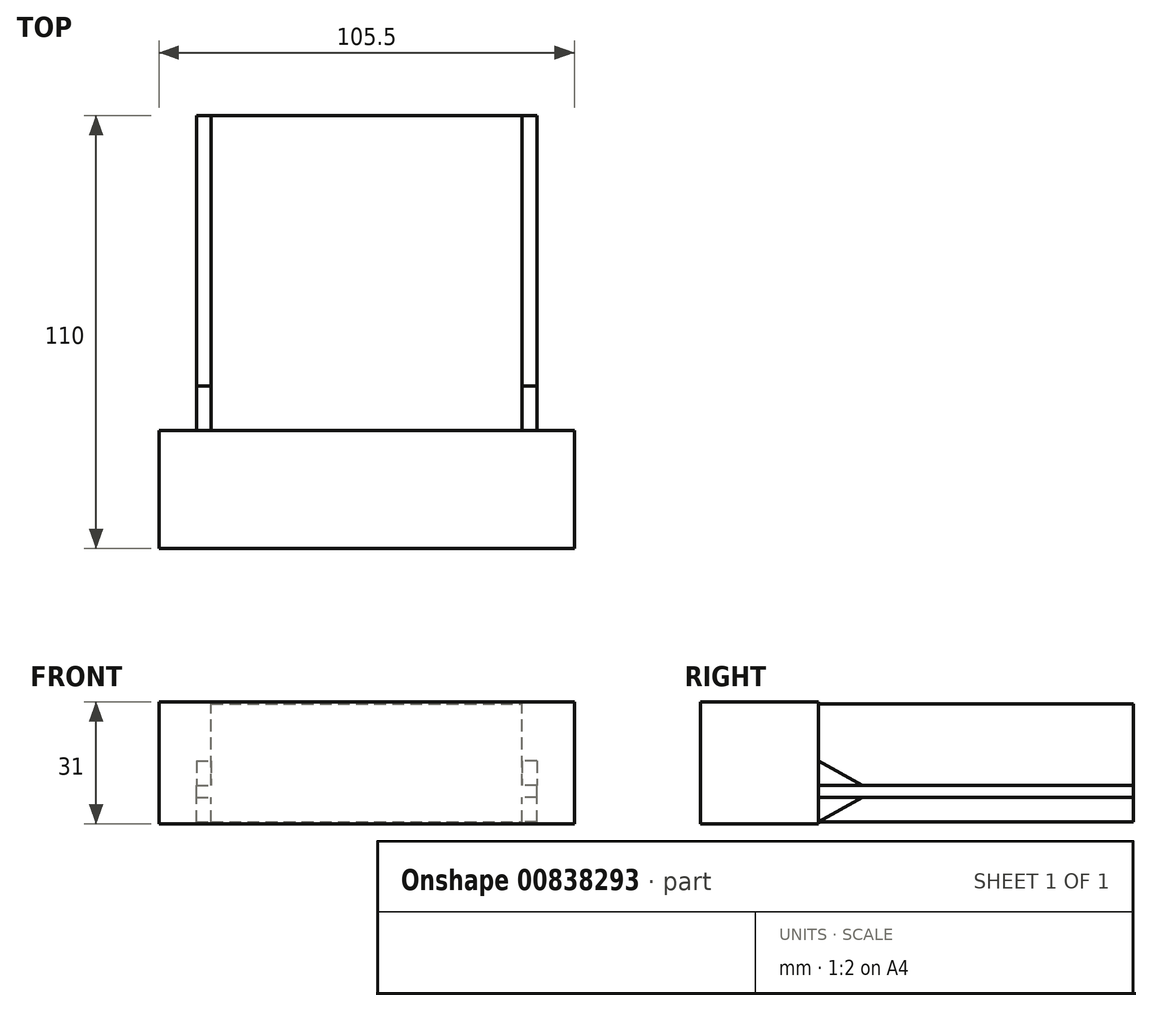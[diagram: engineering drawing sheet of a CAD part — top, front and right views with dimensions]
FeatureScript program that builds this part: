
annotation { "Feature Type Name" : "Feature", "Feature Type Description" : "" }
export const myFeature = defineFeature(function(context is Context, id is Id, definition is map)
    precondition{}
    {
        {
            var Q0;
            Q0=qCreatedBy(makeId("Front.planeOp"),FACE);
            var sketch = newSketch(context, id + "F0", { "sketchPlane" : qUnion([Q0])});
            skLineSegment(sketch, "E0.bottom", {"start": v(-39.5, -15) * mm, "end": v(39.5, -15) * mm});
            skLineSegment(sketch, "E0.top", {"start": v(-39.5, 15) * mm, "end": v(39.5, 15) * mm});
            skLineSegment(sketch, "E0.left", {"start": v(-39.5, -15) * mm, "end": v(-39.5, 15) * mm});
            skLineSegment(sketch, "E0.right", {"start": v(39.5, -15) * mm, "end": v(39.5, 15) * mm});
            skPoint(sketch, "E0.middle", {"position": v(0, 0) * mm});
            skSolve(sketch);
        }
        {
            var Q0;
            Q0=makeQuery(id+"F0.imprint","IMPRINT",FACE,{"disambiguationData":[TD([[makeQuery(id+"F0.imprint","IMPRINT",EDGE,{"derivedFrom":sQuery(id+"F0.wireOp",EDGE,"E0.bottom")}),1.0]])]});
            extrude(context, id + "F1", {"entities" : qUnion([Q0]), "depth" : -80 * mm, "offsetDistance" : 25 * mm});
        }
        {
            var Q0;
            Q0=makeQuery(id+"F1.opExtrude","CAP_FACE",FACE,{"disambiguationData":[OSD([sQuery(id+"F0.wireOp",EDGE,"E0.bottom"),sQuery(id+"F0.wireOp",EDGE,"E0.top"),sQuery(id+"F0.wireOp",EDGE,"E0.left"),sQuery(id+"F0.wireOp",EDGE,"E0.right")])],"isStart":true});
            var sketch = newSketch(context, id + "F2", { "sketchPlane" : qUnion([Q0])});
            skLineSegment(sketch, "E1.bottom", {"start": v(-52.75, 15.5) * mm, "end": v(52.75, 15.5) * mm});
            skLineSegment(sketch, "E1.top", {"start": v(-52.75, -15.5) * mm, "end": v(52.75, -15.5) * mm});
            skLineSegment(sketch, "E1.left", {"start": v(-52.75, 15.5) * mm, "end": v(-52.75, -15.5) * mm});
            skLineSegment(sketch, "E1.right", {"start": v(52.75, 15.5) * mm, "end": v(52.75, -15.5) * mm});
            skPoint(sketch, "E1.middle", {"position": v(0, 0) * mm});
            skSolve(sketch);
        }
        {
            var Q0;
            Q0=makeQuery(id+"F2.imprint","IMPRINT",FACE,{"disambiguationData":[TD([[makeQuery(id+"F2.imprint","IMPRINT",EDGE,{"derivedFrom":sQuery(id+"F2.wireOp",EDGE,"E1.bottom")}),-1.0]])]});
            extrude(context, id + "F3", {"entities" : qUnion([Q0]), "depth" : 30 * mm, "offsetDistance" : 25 * mm});
        }
        {
            var Q0;
            Q0=makeQuery(id+"F2.imprint","IMPRINT",FACE,{"disambiguationData":[TD([[makeQuery(id+"F2.imprint","IMPRINT",EDGE,{"derivedFrom":makeQuery(id+"F1.opExtrude","CAP_EDGE",EDGE,{"disambiguationData":[OSD([sQuery(id+"F0.wireOp",EDGE,"E0.bottom")])],"isStart":true})}),1.0]])]});
            var Q1;
            Q1=makeQuery(id+"F3.opExtrude","CAP_FACE",FACE,{"disambiguationData":[OSD([sQuery(id+"F0.wireOp",EDGE,"E0.bottom"),sQuery(id+"F0.wireOp",EDGE,"E0.top"),sQuery(id+"F0.wireOp",EDGE,"E0.left"),sQuery(id+"F0.wireOp",EDGE,"E0.right"),sQuery(id+"F2.wireOp",EDGE,"E1.bottom"),sQuery(id+"F2.wireOp",EDGE,"E1.top"),sQuery(id+"F2.wireOp",EDGE,"E1.left"),sQuery(id+"F2.wireOp",EDGE,"E1.right")])],"isStart":false});
            extrude(context, id + "F4", {"entities" : qUnion([Q0]), "operationType" : NewBodyOperationType.ADD, "endBound" : BoundingType.UP_TO_SURFACE, "depth" : 25 * mm, "endBoundEntityFace" : qUnion([Q1]), "offsetDistance" : 25 * mm});
        }
        {
            var Q0;
            Q0=qCreatedBy(makeId("Front.planeOp"),FACE);
            var sketch = newSketch(context, id + "F5", { "sketchPlane" : qUnion([Q0])});
            skLineSegment(sketch, "E2", {"start": v(-39.5, -8.75) * mm, "end": v(-43.25, -8.75) * mm});
            skLineSegment(sketch, "E3", {"start": v(-43.25, -8.75) * mm, "end": v(-43.25, -5.75) * mm});
            skLineSegment(sketch, "E4", {"start": v(-43.25, -5.75) * mm, "end": v(-39.5, -5.75) * mm});
            skLineSegment(sketch, "E5", {"start": v(-39.5, -5.75) * mm, "end": v(-39.5, -8.75) * mm});
            skSolve(sketch);
        }
        {
            var Q0;
            Q0=makeQuery(id+"F5.imprint","IMPRINT",FACE,{"disambiguationData":[TD([[makeQuery(id+"F5.imprint","IMPRINT",EDGE,{"derivedFrom":sQuery(id+"F5.wireOp",EDGE,"E2")}),-1.0]])]});
            var Q1;
            Q1=makeQuery(id+"F1.opExtrude","CAP_FACE",FACE,{"disambiguationData":[OSD([sQuery(id+"F0.wireOp",EDGE,"E0.bottom"),sQuery(id+"F0.wireOp",EDGE,"E0.top"),sQuery(id+"F0.wireOp",EDGE,"E0.left"),sQuery(id+"F0.wireOp",EDGE,"E0.right")])],"isStart":false});
            var Q2;
            Q2=makeQuery(id+"F1.opExtrude","SWEPT_BODY",BODY,{"disambiguationData":[OSD([sQuery(id+"F0.wireOp",EDGE,"E0.bottom"),sQuery(id+"F0.wireOp",EDGE,"E0.top"),sQuery(id+"F0.wireOp",EDGE,"E0.left"),sQuery(id+"F0.wireOp",EDGE,"E0.right")])]});
            var Q3;
            Q3 = qBodyType(qCreatedBy(id + "F7" ,FACE), BodyType.SOLID);
            extrude(context, id + "F6", {"entities" : qUnion([Q0]), "oppositeDirection" : true, "depth" : 80 * mm, "endBoundEntityFace" : qUnion([Q1]), "endBoundEntityBody" : qUnion([Q2]), "offsetDistance" : 25 * mm});
        }
        {
            var Q0;
            Q0=makeQuery(id+"F2.imprint","IMPRINT",FACE,{"disambiguationData":[TD([[makeQuery(id+"F2.imprint","IMPRINT",EDGE,{"derivedFrom":makeQuery(id+"F1.opExtrude","CAP_EDGE",EDGE,{"disambiguationData":[OSD([sQuery(id+"F0.wireOp",EDGE,"E0.bottom")])],"isStart":true})}),1.0]])]});
            cPlane(context, id + "F7", {"entities" : qUnion([Q0]), "cplaneType" : CPlaneType.OFFSET, "offset" : 80 * mm, "oppositeDirection" : true, "width" : 150 * mm, "height" : 150 * mm});
        }
        {
            var Q0;
            Q0=makeQuery(id+"F6.opExtrude","SWEPT_BODY",BODY,{"disambiguationData":[OSD([sQuery(id+"F5.wireOp",EDGE,"E2"),sQuery(id+"F5.wireOp",EDGE,"E3"),sQuery(id+"F5.wireOp",EDGE,"E4"),sQuery(id+"F5.wireOp",EDGE,"E5")])]});
            var Q1;
            Q1=makeQuery(id+"F1.opExtrude","SWEPT_FACE",FACE,{"disambiguationData":[OSD([sQuery(id+"F0.wireOp",EDGE,"E0.right")])]});
            mirror(context, id + "F8", {"entities" : qUnion([Q0]), "mirrorPlane" : qUnion([Q1])});
        }
        {
            var Q0;
            Q0=makeQuery(id+"F8.opPattern","COPY",BODY,{"derivedFrom":makeQuery(id+"F6.opExtrude","SWEPT_BODY",BODY,{"disambiguationData":[OSD([sQuery(id+"F5.wireOp",EDGE,"E2"),sQuery(id+"F5.wireOp",EDGE,"E3"),sQuery(id+"F5.wireOp",EDGE,"E4"),sQuery(id+"F5.wireOp",EDGE,"E5")])]}),"instanceName":"1"});
            var Q1;
            Q1=makeQuery(id+"F8.opPattern","COPY",FACE,{"derivedFrom":makeQuery(id+"F6.opExtrude","SWEPT_FACE",FACE,{"disambiguationData":[OSD([sQuery(id+"F5.wireOp",EDGE,"E5")])]}),"instanceName":"1"});
            var Q2;
            Q2=makeQuery(id+"F1.opExtrude","SWEPT_FACE",FACE,{"disambiguationData":[OSD([sQuery(id+"F0.wireOp",EDGE,"E0.right")])]});
            transform(context, id + "F9", {"entities" : qUnion([Q0]), "transformType" : TransformType.TRANSLATION_DISTANCE, "transformDirection" : qUnion([Q1, Q2]), "distance" : 79 * mm, "makeCopy" : false});
        }
        {
            var Q0;
            Q0=makeQuery(id+"F8.opPattern","COPY",BODY,{"derivedFrom":makeQuery(id+"F6.opExtrude","SWEPT_BODY",BODY,{"disambiguationData":[OSD([sQuery(id+"F5.wireOp",EDGE,"E2"),sQuery(id+"F5.wireOp",EDGE,"E3"),sQuery(id+"F5.wireOp",EDGE,"E4"),sQuery(id+"F5.wireOp",EDGE,"E5")])]}),"instanceName":"1"});
            var Q1;
            Q1=makeQuery(id+"F1.opExtrude","SWEPT_BODY",BODY,{"disambiguationData":[OSD([sQuery(id+"F0.wireOp",EDGE,"E0.bottom"),sQuery(id+"F0.wireOp",EDGE,"E0.top"),sQuery(id+"F0.wireOp",EDGE,"E0.left"),sQuery(id+"F0.wireOp",EDGE,"E0.right")])]});
            booleanBodies(context, id + "F10", {"operationType" : BooleanOperationType.UNION, "tools" : qUnion([Q0, Q1])});
        }
        {
            var Q0;
            Q0=makeQuery(id+"F6.opExtrude","SWEPT_BODY",BODY,{"disambiguationData":[OSD([sQuery(id+"F5.wireOp",EDGE,"E2"),sQuery(id+"F5.wireOp",EDGE,"E3"),sQuery(id+"F5.wireOp",EDGE,"E4"),sQuery(id+"F5.wireOp",EDGE,"E5")])]});
            var Q1;
            Q1=makeQuery(id+"F8.opPattern","COPY",BODY,{"derivedFrom":makeQuery(id+"F6.opExtrude","SWEPT_BODY",BODY,{"disambiguationData":[OSD([sQuery(id+"F5.wireOp",EDGE,"E2"),sQuery(id+"F5.wireOp",EDGE,"E3"),sQuery(id+"F5.wireOp",EDGE,"E4"),sQuery(id+"F5.wireOp",EDGE,"E5")])]}),"instanceName":"1"});
            booleanBodies(context, id + "F11", {"operationType" : BooleanOperationType.UNION, "tools" : qUnion([Q0, Q1])});
        }
        {
            var Q0;
            Q0=makeQuery(id+"F6.opExtrude","SWEPT_BODY",BODY,{"disambiguationData":[OSD([sQuery(id+"F5.wireOp",EDGE,"E2"),sQuery(id+"F5.wireOp",EDGE,"E3"),sQuery(id+"F5.wireOp",EDGE,"E4"),sQuery(id+"F5.wireOp",EDGE,"E5")])]});
            transform(context, id + "F12", {"entities" : qUnion([Q0]), "transformType" : TransformType.COPY});
        }
        {
            var Q0;
            Q0=makeQuery(id+"F12.opPattern","COPY",BODY,{"derivedFrom":makeQuery(id+"F6.opExtrude","SWEPT_BODY",BODY,{"disambiguationData":[OSD([sQuery(id+"F5.wireOp",EDGE,"E2"),sQuery(id+"F5.wireOp",EDGE,"E3"),sQuery(id+"F5.wireOp",EDGE,"E4"),sQuery(id+"F5.wireOp",EDGE,"E5")])]}),"instanceName":"1"});
            transform(context, id + "F13", {"entities" : qUnion([Q0]), "transformType" : TransformType.TRANSLATION_3D, "dx" : 0 * mm, "dy" : 0 * mm, "dz" : 0 * mm, "makeCopy" : true});
        }
        {
            var Q0;
            Q0=makeQuery(id+"F13.opPattern","COPY",BODY,{"derivedFrom":makeQuery(id+"F12.opPattern","COPY",BODY,{"derivedFrom":makeQuery(id+"F6.opExtrude","SWEPT_BODY",BODY,{"disambiguationData":[OSD([sQuery(id+"F5.wireOp",EDGE,"E2"),sQuery(id+"F5.wireOp",EDGE,"E3"),sQuery(id+"F5.wireOp",EDGE,"E4"),sQuery(id+"F5.wireOp",EDGE,"E5")])]}),"instanceName":"1"}),"instanceName":"1"});
            deleteBodies(context, id + "F14", {"entities" : qUnion([Q0])});
        }
        {
            var Q0;
            Q0=makeQuery(id+"F12.opPattern","COPY",BODY,{"derivedFrom":makeQuery(id+"F6.opExtrude","SWEPT_BODY",BODY,{"disambiguationData":[OSD([sQuery(id+"F5.wireOp",EDGE,"E2"),sQuery(id+"F5.wireOp",EDGE,"E3"),sQuery(id+"F5.wireOp",EDGE,"E4"),sQuery(id+"F5.wireOp",EDGE,"E5")])]}),"instanceName":"1"});
            deleteBodies(context, id + "F15", {"entities" : qUnion([Q0])});
        }
        {
            var Q0;
            {var subQ1=sQuery(id+"F0.wireOp",EDGE,"E0.left");var subQ3=sQuery(id+"F0.wireOp",EDGE,"E0.bottom");Q0=makeQuery(id+"F11.opBoolean","SPLIT",FACE,{"disambiguationData":[TD([makeQuery(id+"F1.opExtrude","SWEPT_FACE",FACE,{"disambiguationData":[OSD([subQ3])]})])],"derivedFrom":makeQuery(id+"F1.opExtrude","SWEPT_FACE",FACE,{"disambiguationData":[OSD([subQ1])]})});}
            var sketch = newSketch(context, id + "F16", { "sketchPlane" : qUnion([Q0])});
            skSolve(sketch);
        }
        {
            var Q0;
            {var subQ0=sQuery(id+"F0.wireOp",EDGE,"E0.right");var subQ3=sQuery(id+"F0.wireOp",EDGE,"E0.bottom");Q0=makeQuery(id+"F10.opBoolean","SPLIT",FACE,{"disambiguationData":[TD([makeQuery(id+"F1.opExtrude","SWEPT_FACE",FACE,{"disambiguationData":[OSD([subQ3])]})])],"derivedFrom":makeQuery(id+"F1.opExtrude","SWEPT_FACE",FACE,{"disambiguationData":[OSD([subQ0])]})});}
            var sketch = newSketch(context, id + "F17", { "sketchPlane" : qUnion([Q0])});
            skLineSegment(sketch, "E6", {"start": v(0, -15) * mm, "end": v(11.24, -8.75) * mm});
            skLineSegment(sketch, "E7", {"start": v(11.24, -8.75) * mm, "end": v(0, -8.75) * mm});
            skLineSegment(sketch, "E8", {"start": v(0, -8.75) * mm, "end": v(0, -15) * mm});
            skSolve(sketch);
        }
        {
            var Q0;
            Q0=makeQuery(id+"F17.imprint","IMPRINT",FACE,{"disambiguationData":[TD([[makeQuery(id+"F17.imprint","IMPRINT",EDGE,{"derivedFrom":sQuery(id+"F17.wireOp",EDGE,"E6")}),1.0]])]});
            extrude(context, id + "F18", {"entities" : qUnion([Q0]), "depth" : 3.75 * mm, "offsetDistance" : 25 * mm});
        }
        {
            var Q0;
            Q0=makeQuery(id+"F18.opExtrude","SWEPT_BODY",BODY,{"disambiguationData":[OSD([sQuery(id+"F17.wireOp",EDGE,"E6"),sQuery(id+"F17.wireOp",EDGE,"E7"),sQuery(id+"F17.wireOp",EDGE,"E8")])]});
            var Q1;
            {var subQ1=sQuery(id+"F0.wireOp",EDGE,"E0.left");var subQ2=sQuery(id+"F0.wireOp",EDGE,"E0.top");Q1=makeQuery(id+"F11.opBoolean","SPLIT",FACE,{"disambiguationData":[TD([makeQuery(id+"F1.opExtrude","SWEPT_FACE",FACE,{"disambiguationData":[OSD([subQ2])]})])],"derivedFrom":makeQuery(id+"F1.opExtrude","SWEPT_FACE",FACE,{"disambiguationData":[OSD([subQ1])]})});}
            mirror(context, id + "F19", {"entities" : qUnion([Q0]), "mirrorPlane" : qUnion([Q1])});
        }
        {
            var Q0;
            Q0=makeQuery(id+"F19.opPattern","COPY",BODY,{"derivedFrom":makeQuery(id+"F18.opExtrude","SWEPT_BODY",BODY,{"disambiguationData":[OSD([sQuery(id+"F17.wireOp",EDGE,"E6"),sQuery(id+"F17.wireOp",EDGE,"E7"),sQuery(id+"F17.wireOp",EDGE,"E8")])]}),"instanceName":"1"});
            var Q1;
            Q1=makeQuery(id+"F19.opPattern","COPY",FACE,{"derivedFrom":makeQuery(id+"F18.opExtrude","CAP_FACE",FACE,{"disambiguationData":[OSD([sQuery(id+"F17.wireOp",EDGE,"E6"),sQuery(id+"F17.wireOp",EDGE,"E7"),sQuery(id+"F17.wireOp",EDGE,"E8")])],"isStart":true}),"instanceName":"1"});
            var Q2;
            {var subQ0=sQuery(id+"F0.wireOp",EDGE,"E0.left");var subQ1=sQuery(id+"F0.wireOp",EDGE,"E0.bottom");Q2=makeQuery(id+"F16.imprint","IMPRINT",FACE,{"disambiguationData":[TD([[makeQuery(id+"F16.imprint","IMPRINT",EDGE,{"derivedFrom":makeQuery(id+"F1.opExtrude","SWEPT_EDGE",EDGE,{"disambiguationData":[OSD([subQ1,subQ0])]})}),1.0]])]});}
            transform(context, id + "F20", {"entities" : qUnion([Q0]), "transformType" : TransformType.TRANSLATION_DISTANCE, "transformDirection" : qUnion([Q1, Q2]), "distance" : 79 * mm, "makeCopy" : false});
        }
        {
            var Q0;
            Q0=makeQuery(id+"F19.opPattern","COPY",BODY,{"derivedFrom":makeQuery(id+"F18.opExtrude","SWEPT_BODY",BODY,{"disambiguationData":[OSD([sQuery(id+"F17.wireOp",EDGE,"E6"),sQuery(id+"F17.wireOp",EDGE,"E7"),sQuery(id+"F17.wireOp",EDGE,"E8")])]}),"instanceName":"1"});
            var Q1;
            Q1=makeQuery(id+"F6.opExtrude","SWEPT_FACE",FACE,{"disambiguationData":[OSD([sQuery(id+"F5.wireOp",EDGE,"E4")])]});
            mirror(context, id + "F21", {"entities" : qUnion([Q0]), "mirrorPlane" : qUnion([Q1])});
        }
        {
            var Q0;
            Q0=makeQuery(id+"F21.opPattern","COPY",BODY,{"derivedFrom":makeQuery(id+"F19.opPattern","COPY",BODY,{"derivedFrom":makeQuery(id+"F18.opExtrude","SWEPT_BODY",BODY,{"disambiguationData":[OSD([sQuery(id+"F17.wireOp",EDGE,"E6"),sQuery(id+"F17.wireOp",EDGE,"E7"),sQuery(id+"F17.wireOp",EDGE,"E8")])]}),"instanceName":"1"}),"instanceName":"1"});
            var Q1;
            Q1=makeQuery(id+"F6.opExtrude","SWEPT_FACE",FACE,{"disambiguationData":[OSD([sQuery(id+"F5.wireOp",EDGE,"E4")])]});
            var Q2;
            Q2=makeQuery(id+"F21.opPattern","COPY",FACE,{"derivedFrom":makeQuery(id+"F19.opPattern","COPY",FACE,{"derivedFrom":makeQuery(id+"F18.opExtrude","SWEPT_FACE",FACE,{"disambiguationData":[OSD([sQuery(id+"F17.wireOp",EDGE,"E7")])]}),"instanceName":"1"}),"instanceName":"1"});
            transform(context, id + "F22", {"entities" : qUnion([Q0]), "transformType" : TransformType.TRANSLATION_DISTANCE, "transformDirection" : qUnion([Q1, Q2]), "distance" : 3 * mm, "oppositeDirection" : true, "makeCopy" : false});
        }
        {
            var Q0;
            Q0=makeQuery(id+"F18.opExtrude","SWEPT_BODY",BODY,{"disambiguationData":[OSD([sQuery(id+"F17.wireOp",EDGE,"E6"),sQuery(id+"F17.wireOp",EDGE,"E7"),sQuery(id+"F17.wireOp",EDGE,"E8")])]});
            var Q1;
            Q1=makeQuery(id+"F8.opPattern","COPY",FACE,{"derivedFrom":makeQuery(id+"F6.opExtrude","SWEPT_FACE",FACE,{"disambiguationData":[OSD([sQuery(id+"F5.wireOp",EDGE,"E4")])]}),"instanceName":"1"});
            mirror(context, id + "F23", {"entities" : qUnion([Q0]), "mirrorPlane" : qUnion([Q1])});
        }
        {
            var Q0;
            Q0=makeQuery(id+"F23.opPattern","COPY",BODY,{"derivedFrom":makeQuery(id+"F18.opExtrude","SWEPT_BODY",BODY,{"disambiguationData":[OSD([sQuery(id+"F17.wireOp",EDGE,"E6"),sQuery(id+"F17.wireOp",EDGE,"E7"),sQuery(id+"F17.wireOp",EDGE,"E8")])]}),"instanceName":"1"});
            var Q1;
            Q1=makeQuery(id+"F23.opPattern","COPY",FACE,{"derivedFrom":makeQuery(id+"F18.opExtrude","SWEPT_FACE",FACE,{"disambiguationData":[OSD([sQuery(id+"F17.wireOp",EDGE,"E7")])]}),"instanceName":"1"});
            var Q2;
            Q2=makeQuery(id+"F8.opPattern","COPY",FACE,{"derivedFrom":makeQuery(id+"F6.opExtrude","SWEPT_FACE",FACE,{"disambiguationData":[OSD([sQuery(id+"F5.wireOp",EDGE,"E4")])]}),"instanceName":"1"});
            transform(context, id + "F24", {"entities" : qUnion([Q0]), "transformType" : TransformType.TRANSLATION_DISTANCE, "transformDirection" : qUnion([Q1, Q2]), "distance" : 3 * mm, "makeCopy" : false});
        }
    });
